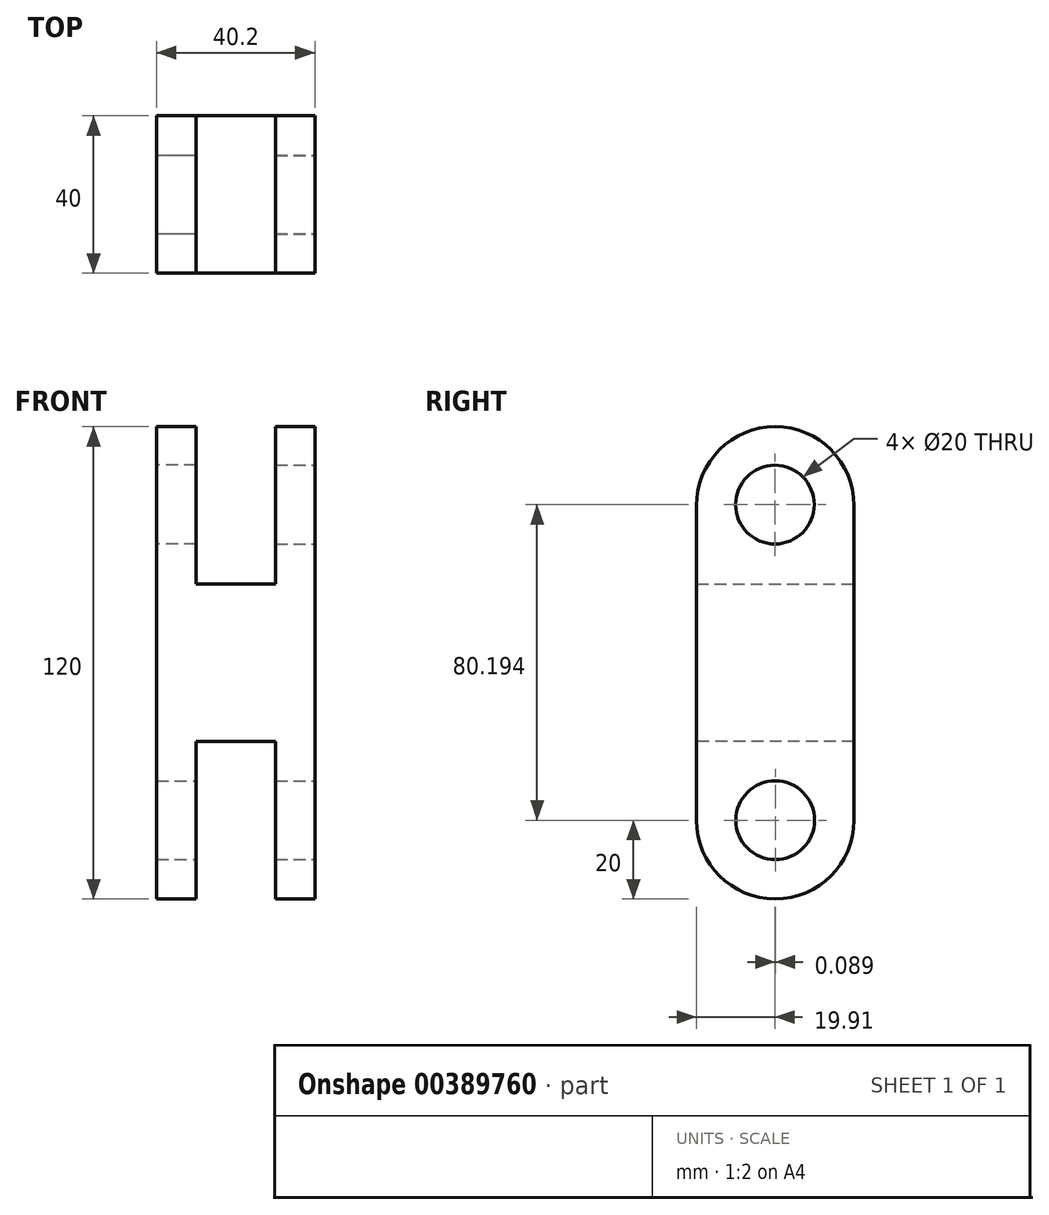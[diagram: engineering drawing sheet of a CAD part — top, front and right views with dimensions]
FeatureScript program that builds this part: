
annotation { "Feature Type Name" : "Feature", "Feature Type Description" : "" }
export const myFeature = defineFeature(function(context is Context, id is Id, definition is map)
    precondition{}
    {
        {
            var Q0;
            Q0=qCreatedBy(makeId("Right.planeOp"),FACE);
            var sketch = newSketch(context, id + "F0", { "sketchPlane" : qUnion([Q0])});
            skLineSegment(sketch, "E0.bottom", {"start": v(-20, 40) * mm, "end": v(20, 40) * mm});
            skLineSegment(sketch, "E0.top", {"start": v(-20, -40) * mm, "end": v(20, -40) * mm});
            skLineSegment(sketch, "E0.left", {"start": v(-20, 40) * mm, "end": v(-20, -40) * mm});
            skLineSegment(sketch, "E0.right", {"start": v(20, 40) * mm, "end": v(20, -40) * mm});
            skPoint(sketch, "E0.middle", {"position": v(0, 0) * mm});
            skSolve(sketch);
        }
        {
            var Q0;
            Q0 = qSketchRegion(id + "F0", true);
            extrude(context, id + "F1", {"entities" : qUnion([Q0]), "depth" : 20.1 * mm});
        }
        {
            var Q0;
            Q0=makeQuery(id+"F1.opExtrude","CAP_FACE",FACE,{"disambiguationData":[OSD([sQuery(id+"F0.wireOp",EDGE,"E0.bottom"),sQuery(id+"F0.wireOp",EDGE,"E0.top"),sQuery(id+"F0.wireOp",EDGE,"E0.left"),sQuery(id+"F0.wireOp",EDGE,"E0.right")])],"isStart":false});
            var sketch = newSketch(context, id + "F2", { "sketchPlane" : qUnion([Q0])});
            skLineSegment(sketch, "E1.bottom", {"start": v(-20, 40) * mm, "end": v(20, 40) * mm});
            skLineSegment(sketch, "E1.left", {"start": v(-20, 40) * mm, "end": v(-20, 60) * mm});
            skLineSegment(sketch, "E1.right", {"start": v(20, 40) * mm, "end": v(20, 60) * mm});
            skArc(sketch, "E2", {"start": v(20, 60) * mm, "mid": v(0, 80) * mm, "end": v(-20, 60) * mm});
            skCircle(sketch, "E3", {"center": v(-0.09, 60.2) * mm, "radius": 10 * mm});
            skSolve(sketch);
        }
        {
            var Q0;
            Q0 = qSketchRegion(id + "F2", true);
            extrude(context, id + "F3", {"entities" : qUnion([Q0]), "operationType" : NewBodyOperationType.ADD, "oppositeDirection" : true, "depth" : 10 * mm});
        }
        {
            var Q0;
            Q0=makeQuery(id+"F1.opExtrude","SWEPT_BODY",BODY,{"disambiguationData":[OSD([sQuery(id+"F0.wireOp",EDGE,"E0.bottom"),sQuery(id+"F0.wireOp",EDGE,"E0.top"),sQuery(id+"F0.wireOp",EDGE,"E0.left"),sQuery(id+"F0.wireOp",EDGE,"E0.right")])]});
            var Q1;
            Q1=makeQuery(id+"F1.opExtrude","CAP_FACE",FACE,{"disambiguationData":[OSD([sQuery(id+"F0.wireOp",EDGE,"E0.bottom"),sQuery(id+"F0.wireOp",EDGE,"E0.top"),sQuery(id+"F0.wireOp",EDGE,"E0.left"),sQuery(id+"F0.wireOp",EDGE,"E0.right")])],"isStart":true});
            mirror(context, id + "F4", {"operationType" : NewBodyOperationType.ADD, "entities" : qUnion([Q0]), "mirrorPlane" : qUnion([Q1])});
        }
        {
            var Q0;
            Q0=qCreatedBy(makeId("Front.planeOp"),FACE);
            var sketch = newSketch(context, id + "F5", { "sketchPlane" : qUnion([Q0])});
            skLineSegment(sketch, "E4.bottom", {"start": v(-10.1, -40) * mm, "end": v(10.1, -40) * mm});
            skLineSegment(sketch, "E4.top", {"start": v(-10.1, 0) * mm, "end": v(10.1, 0) * mm});
            skLineSegment(sketch, "E4.left", {"start": v(-10.1, -40) * mm, "end": v(-10.1, 0) * mm});
            skLineSegment(sketch, "E4.right", {"start": v(10.1, -40) * mm, "end": v(10.1, 0) * mm});
            skSolve(sketch);
        }
        {
            var Q0;
            Q0 = qSketchRegion(id + "F5", true);
            var Q1;
            {var subQ0=makeQuery(id+"F3.boolean.opBoolean","MERGE",FACE,{"derivedFrom":[makeQuery(id+"F1.opExtrude","SWEPT_FACE",FACE,{"disambiguationData":[OSD([sQuery(id+"F0.wireOp",EDGE,"E0.right")])]}),makeQuery(id+"F3.opExtrude","SWEPT_FACE",FACE,{"disambiguationData":[OSD([sQuery(id+"F2.wireOp",EDGE,"E1.right")])]})]});Q1=makeQuery(id+"F4.boolean.opBoolean","MERGE",FACE,{"derivedFrom":[subQ0,makeQuery(id+"F4.opPattern","COPY",FACE,{"derivedFrom":subQ0,"instanceName":"1"})]});}
            extrude(context, id + "F6", {"entities" : qUnion([Q0]), "operationType" : NewBodyOperationType.REMOVE, "endBound" : BoundingType.SYMMETRIC, "oppositeDirection" : true, "endBoundEntityFace" : qUnion([Q1]), "depth" : 40.2 * mm});
        }
        {
            var Q0;
            Q0=makeQuery(id+"F3.boolean.opBoolean","MERGE",FACE,{"derivedFrom":[makeQuery(id+"F1.opExtrude","CAP_FACE",FACE,{"disambiguationData":[OSD([sQuery(id+"F0.wireOp",EDGE,"E0.bottom"),sQuery(id+"F0.wireOp",EDGE,"E0.top"),sQuery(id+"F0.wireOp",EDGE,"E0.left"),sQuery(id+"F0.wireOp",EDGE,"E0.right")])],"isStart":false}),makeQuery(id+"F3.opExtrude","CAP_FACE",FACE,{"disambiguationData":[OSD([sQuery(id+"F2.wireOp",EDGE,"E1.bottom"),sQuery(id+"F2.wireOp",EDGE,"E1.left"),sQuery(id+"F2.wireOp",EDGE,"E1.right"),sQuery(id+"F2.wireOp",EDGE,"E2"),sQuery(id+"F2.wireOp",EDGE,"E3")])],"isStart":true})]});
            var sketch = newSketch(context, id + "F7", { "sketchPlane" : qUnion([Q0])});
            skLineSegment(sketch, "E5", {"start": v(0, -40) * mm, "end": v(0, -20) * mm, "construction": true});
            skPoint(sketch, "E5.endSnap0", {"position": v(0, -40) * mm});
            skCircle(sketch, "E6", {"center": v(0, -20) * mm, "radius": 10 * mm});
            skSolve(sketch);
        }
        {
            var Q0;
            Q0=makeQuery(id+"F7.imprint","IMPRINT",FACE,{"disambiguationData":[TD([[makeQuery(id+"F7.imprint","IMPRINT",EDGE,{"derivedFrom":sQuery(id+"F7.wireOp",EDGE,"E6")}),1.0]])]});
            extrude(context, id + "F8", {"entities" : qUnion([Q0]), "operationType" : NewBodyOperationType.REMOVE, "oppositeDirection" : true, "depth" : 40.2 * mm});
        }
        {
            var Q0;
            {var subQ0=sQuery(id+"F0.wireOp",EDGE,"E0.top");var subQ4=sQuery(id+"F0.wireOp",EDGE,"E0.left");var subQ6=makeQuery(id+"F1.opExtrude","SWEPT_EDGE",EDGE,{"disambiguationData":[OSD([subQ0,subQ4])]});Q0=makeQuery(id+"F6.boolean.opBoolean","SPLIT",EDGE,{"disambiguationData":[TD([makeQuery(id+"F6.opExtrude","SWEPT_FACE",FACE,{"disambiguationData":[OSD([sQuery(id+"F5.wireOp",EDGE,"E4.left")])]})])],"derivedFrom":makeQuery(id+"F4.boolean.opBoolean","MERGE",EDGE,{"derivedFrom":[subQ6,makeQuery(id+"F4.opPattern","COPY",EDGE,{"derivedFrom":subQ6,"instanceName":"1"})]})});}
            var Q1;
            {var subQ1=sQuery(id+"F0.wireOp",EDGE,"E0.left");var subQ2=sQuery(id+"F0.wireOp",EDGE,"E0.top");var subQ6=makeQuery(id+"F1.opExtrude","SWEPT_EDGE",EDGE,{"disambiguationData":[OSD([subQ2,subQ1])]});Q1=makeQuery(id+"F6.boolean.opBoolean","SPLIT",EDGE,{"disambiguationData":[TD([makeQuery(id+"F6.opExtrude","SWEPT_FACE",FACE,{"disambiguationData":[OSD([sQuery(id+"F5.wireOp",EDGE,"E4.right")])]})])],"derivedFrom":makeQuery(id+"F4.boolean.opBoolean","MERGE",EDGE,{"derivedFrom":[subQ6,makeQuery(id+"F4.opPattern","COPY",EDGE,{"derivedFrom":subQ6,"instanceName":"1"})]})});}
            var Q2;
            {var subQ1=sQuery(id+"F0.wireOp",EDGE,"E0.right");var subQ2=sQuery(id+"F0.wireOp",EDGE,"E0.top");var subQ6=makeQuery(id+"F1.opExtrude","SWEPT_EDGE",EDGE,{"disambiguationData":[OSD([subQ2,subQ1])]});Q2=makeQuery(id+"F6.boolean.opBoolean","SPLIT",EDGE,{"disambiguationData":[TD([makeQuery(id+"F6.opExtrude","SWEPT_FACE",FACE,{"disambiguationData":[OSD([sQuery(id+"F5.wireOp",EDGE,"E4.right")])]})])],"derivedFrom":makeQuery(id+"F4.boolean.opBoolean","MERGE",EDGE,{"derivedFrom":[subQ6,makeQuery(id+"F4.opPattern","COPY",EDGE,{"derivedFrom":subQ6,"instanceName":"1"})]})});}
            var Q3;
            {var subQ0=sQuery(id+"F0.wireOp",EDGE,"E0.top");var subQ4=sQuery(id+"F0.wireOp",EDGE,"E0.right");var subQ6=makeQuery(id+"F1.opExtrude","SWEPT_EDGE",EDGE,{"disambiguationData":[OSD([subQ0,subQ4])]});Q3=makeQuery(id+"F6.boolean.opBoolean","SPLIT",EDGE,{"disambiguationData":[TD([makeQuery(id+"F6.opExtrude","SWEPT_FACE",FACE,{"disambiguationData":[OSD([sQuery(id+"F5.wireOp",EDGE,"E4.left")])]})])],"derivedFrom":makeQuery(id+"F4.boolean.opBoolean","MERGE",EDGE,{"derivedFrom":[subQ6,makeQuery(id+"F4.opPattern","COPY",EDGE,{"derivedFrom":subQ6,"instanceName":"1"})]})});}
            fillet(context, id + "F9", {"entities" : qUnion([Q0, Q1, Q2, Q3]), "radius" : 20 * mm, "tangentPropagation" : true, "allowEdgeOverflow" : false});
        }
    });
